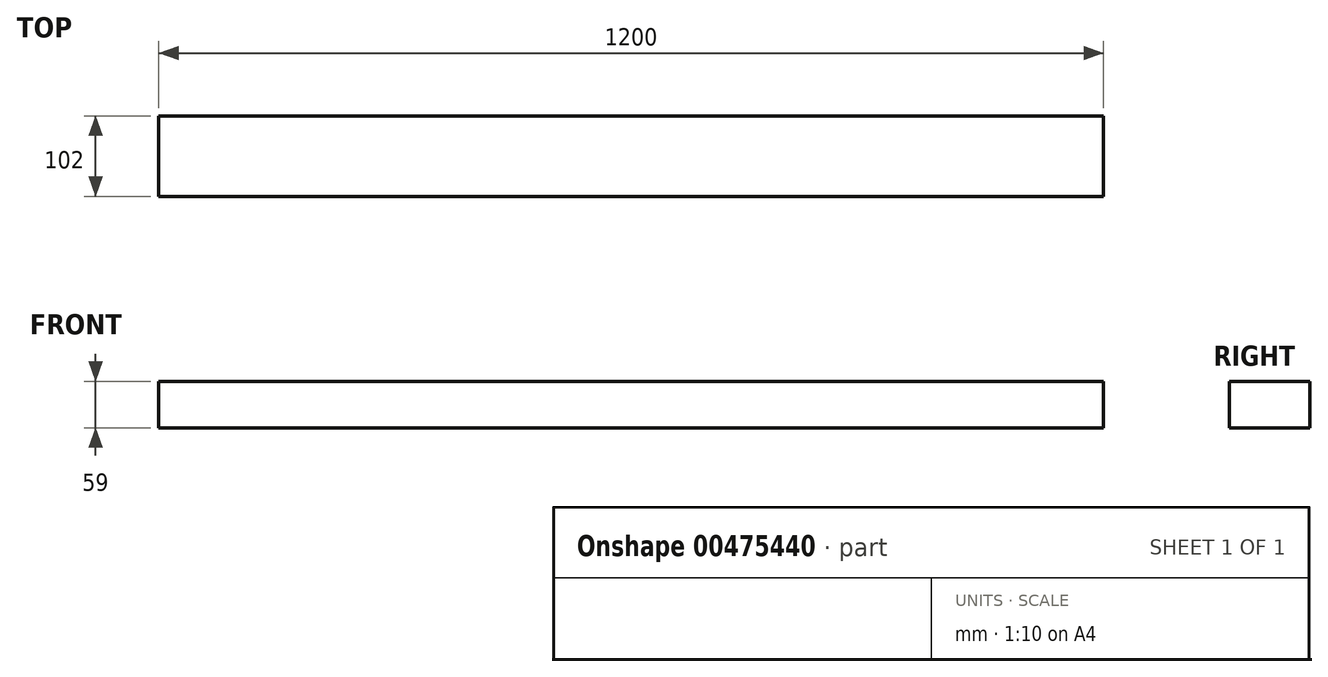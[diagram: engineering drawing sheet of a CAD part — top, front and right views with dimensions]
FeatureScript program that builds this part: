
annotation { "Feature Type Name" : "Feature", "Feature Type Description" : "" }
export const myFeature = defineFeature(function(context is Context, id is Id, definition is map)
    precondition{}
    {
        {
            var Q0;
            Q0=qCreatedBy(makeId("Top.planeOp"),FACE);
            var sketch = newSketch(context, id + "F0", { "sketchPlane" : qUnion([Q0])});
            skLineSegment(sketch, "E0.bottom", {"start": v(-600, 51) * mm, "end": v(600, 51) * mm});
            skLineSegment(sketch, "E0.top", {"start": v(-600, -51) * mm, "end": v(600, -51) * mm});
            skLineSegment(sketch, "E0.left", {"start": v(-600, 51) * mm, "end": v(-600, -51) * mm});
            skLineSegment(sketch, "E0.right", {"start": v(600, 51) * mm, "end": v(600, -51) * mm});
            skPoint(sketch, "E0.middle", {"position": v(0, 0) * mm});
            skSolve(sketch);
        }
        {
            var Q0;
            Q0 = qSketchRegion(id + "F0", true);
            extrude(context, id + "F1", {"entities" : qUnion([Q0]), "depth" : 59 * mm});
        }
    });
